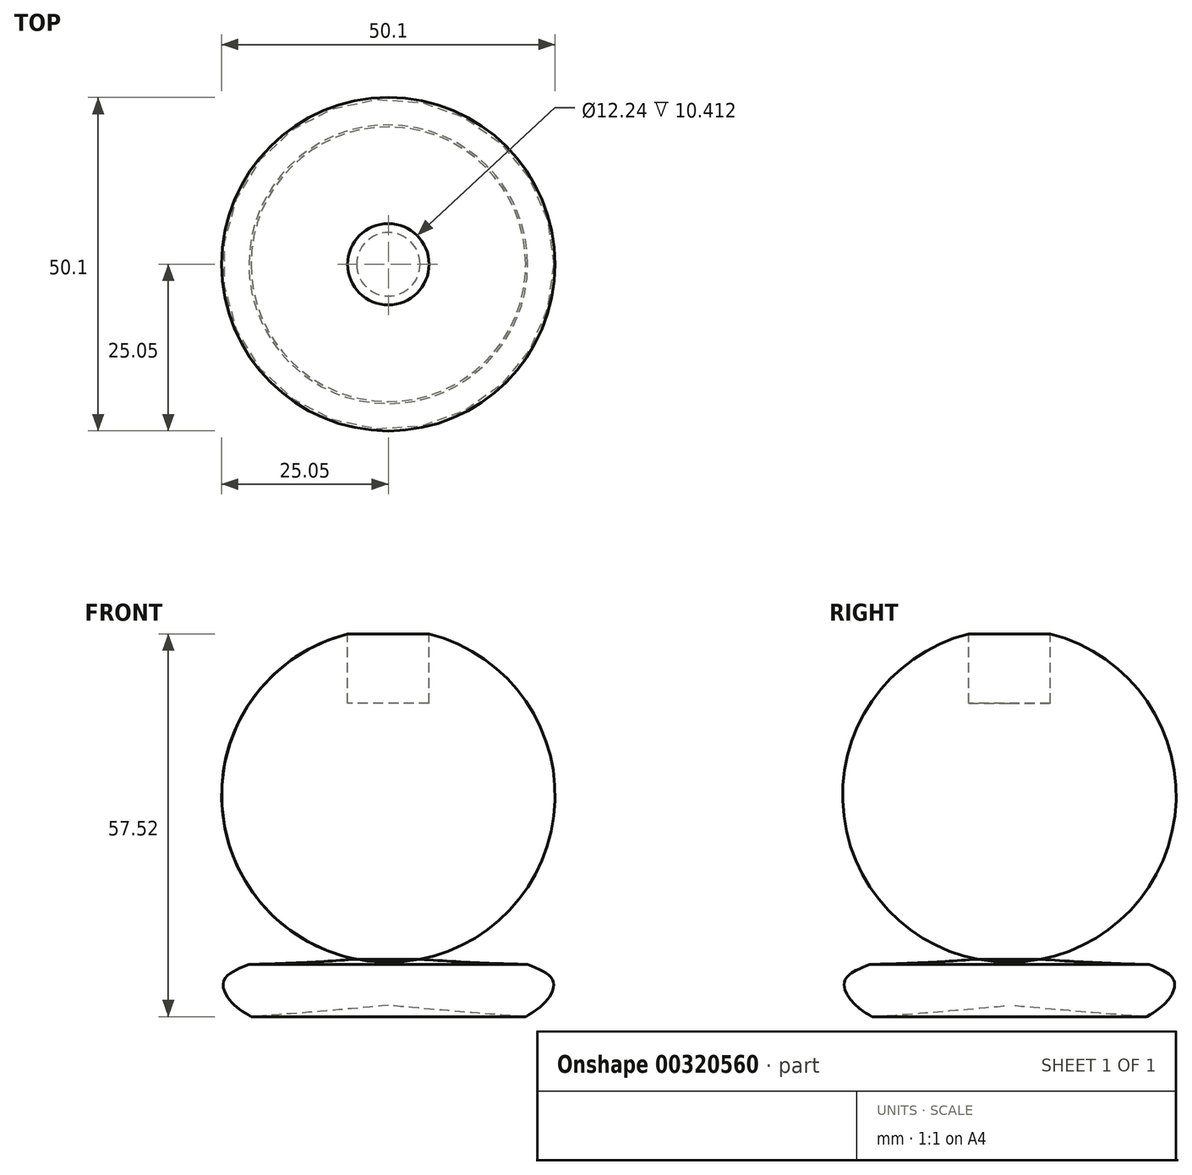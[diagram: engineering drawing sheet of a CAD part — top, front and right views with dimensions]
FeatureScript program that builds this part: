
annotation { "Feature Type Name" : "Feature", "Feature Type Description" : "" }
export const myFeature = defineFeature(function(context is Context, id is Id, definition is map)
    precondition{}
    {
        {
            var Q0;
            Q0=qCreatedBy(makeId("Front.planeOp"),FACE);
            var sketch = newSketch(context, id + "F0", { "sketchPlane" : qUnion([Q0])});
            skFitSpline(sketch, "E0", {"points": [v(0, -64.95) * mm, v(-42.36, -65.18) * mm, v(-39.06, -60.95) * mm, v(-30.12, -59.07) * mm, v(-14.6, -58.6) * mm, v(0, -57.65) * mm], "startDerivative": vector(-184.56, -16.5) * mm, "endDerivative": vector(72.87, 5.62) * mm});
            skArc(sketch, "E1", {"start": v(-6.82, -9.3) * mm, "mid": v(0.37, -58.47) * mm, "end": v(6.12, -9.12) * mm});
            skFitSpline(sketch, "E2", {"points": [v(-20.94, -58.8) * mm, v(-24.7, -61.18) * mm, v(-23.77, -64.24) * mm, v(-20.41, -66.77) * mm], "startDerivative": vector(-14.1, -5.55) * mm, "endDerivative": vector(10.7, -6.32) * mm});
            skLineSegment(sketch, "E3", {"start": v(0, 71.54) * mm, "end": v(0, -76) * mm});
            skLineSegment(sketch, "E4", {"start": v(-6.82, -9.3) * mm, "end": v(-6.82, -19.53) * mm});
            skPoint(sketch, "E4.startSnap0", {"position": v(0, -2.24) * mm});
            skLineSegment(sketch, "E5", {"start": v(-6.82, -19.53) * mm, "end": v(6.12, -19.53) * mm});
            skLineSegment(sketch, "E6", {"start": v(6.12, -19.53) * mm, "end": v(6.12, -9.12) * mm});
            skPoint(sketch, "E7.orphan", {"position": v(-6.82, -2.24) * mm});
            skSolve(sketch);
        }
        {
            var Q0;
            {var subQ0=sQuery(id+"F0.wireOp",EDGE,"E3");var subQ1=sQuery(id+"F0.wireOp",EDGE,"E1");var subQ2=makeQuery(id+"F0.imprint","INTERSECT",VERTEX,{"disambiguationData":[OD(0.0)],"derivedFrom":[subQ1,subQ0]});Q0=makeQuery(id+"F0.imprint","IMPRINT",FACE,{"disambiguationData":[TD([[makeQuery(id+"F0.imprint","IMPRINT",EDGE,{"disambiguationData":[TD([[subQ2,-1.0]])],"derivedFrom":subQ1}),1.0]])]});}
            var Q1;
            {var subQ1=sQuery(id+"F0.wireOp",EDGE,"E0");Q1=makeQuery(id+"F0.imprint","IMPRINT",FACE,{"disambiguationData":[TD([[makeQuery(id+"F0.imprint","IMPRINT",EDGE,{"derivedFrom":subQ1}),-1.0]])]});}
            var Q2;
            Q2=sQuery(id+"F0.wireOp",EDGE,"E3");
            revolve(context, id + "F1", {"entities" : qUnion([Q0, Q1]), "axis" : qUnion([Q2]), "revolveType" : RevolveType.FULL});
        }
    });
